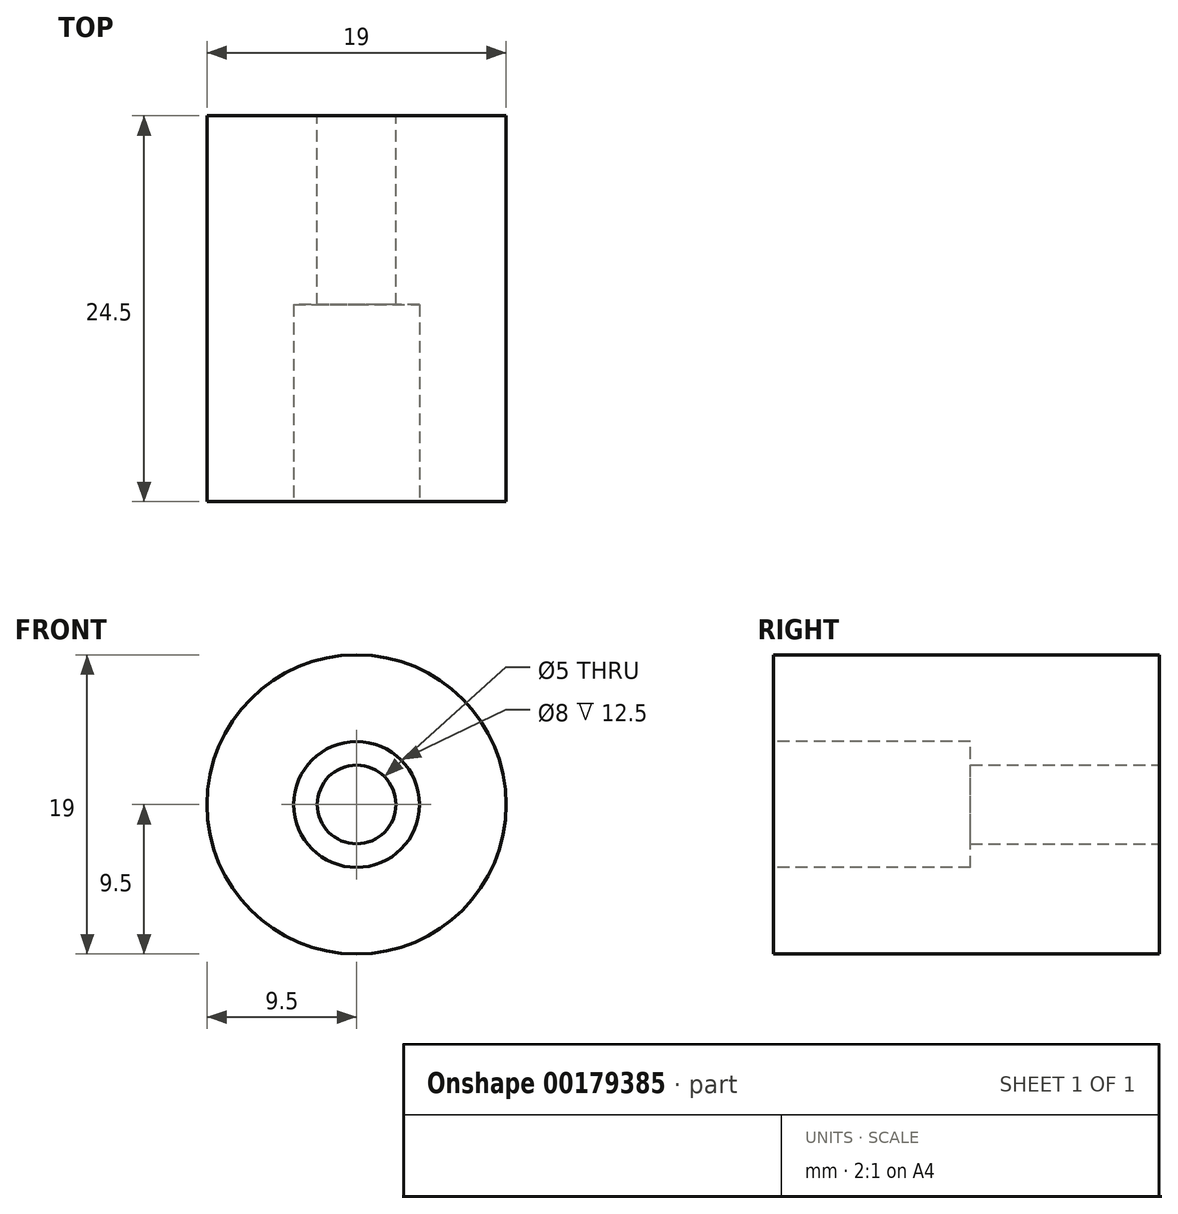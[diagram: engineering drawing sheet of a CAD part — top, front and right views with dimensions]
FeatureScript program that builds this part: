
annotation { "Feature Type Name" : "Feature", "Feature Type Description" : "" }
export const myFeature = defineFeature(function(context is Context, id is Id, definition is map)
    precondition{}
    {
        {
            var Q0;
            Q0=qCreatedBy(makeId("Front.planeOp"),FACE);
            var sketch = newSketch(context, id + "F0", { "sketchPlane" : qUnion([Q0])});
            skCircle(sketch, "E0", {"center": v(0, 0) * mm, "radius": 9.5 * mm});
            skCircle(sketch, "E1", {"center": v(0, 0) * mm, "radius": 2.5 * mm});
            skSolve(sketch);
        }
        {
            var Q0;
            Q0 = qSketchRegion(id + "F0", true);
            extrude(context, id + "F1", {"entities" : qUnion([Q0]), "depth" : 24.5 * mm});
        }
        {
            var Q0;
            Q0=makeQuery(id+"F1.opExtrude","CAP_FACE",FACE,{"disambiguationData":[OSD([sQuery(id+"F0.wireOp",EDGE,"E0")])],"isStart":false});
            var sketch = newSketch(context, id + "F2", { "sketchPlane" : qUnion([Q0])});
            skCircle(sketch, "E2", {"center": v(0, 0) * mm, "radius": 4 * mm});
            skSolve(sketch);
        }
        {
            var Q0;
            Q0 = qSketchRegion(id + "F2", true);
            extrude(context, id + "F3", {"entities" : qUnion([Q0]), "operationType" : NewBodyOperationType.REMOVE, "oppositeDirection" : true, "depth" : 12.5 * mm});
        }
    });
